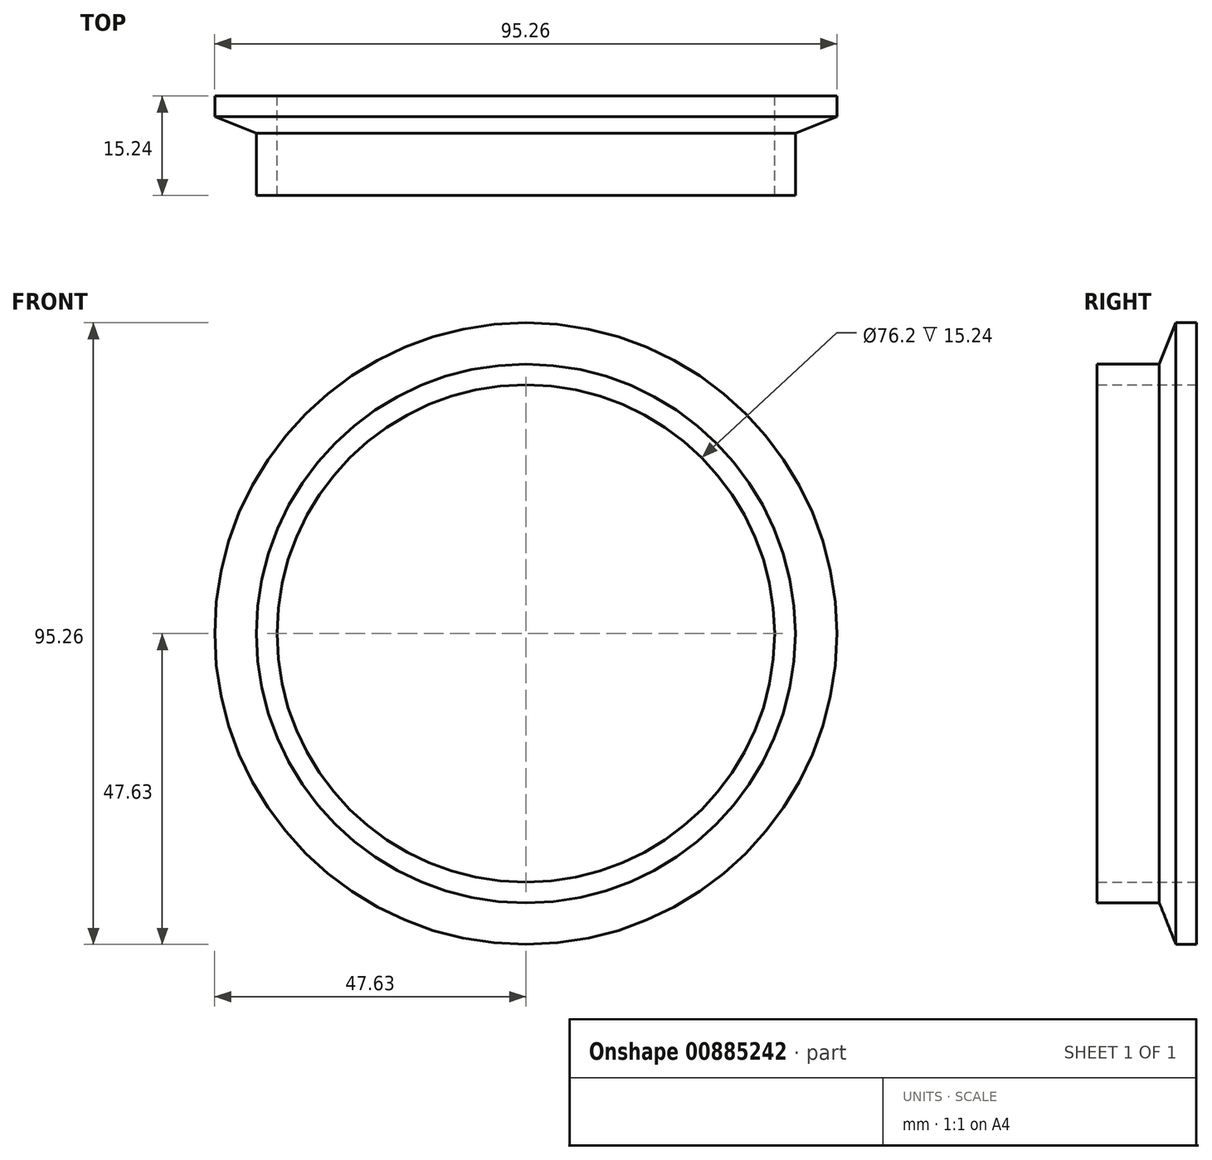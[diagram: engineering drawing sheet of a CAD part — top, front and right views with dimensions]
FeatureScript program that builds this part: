
annotation { "Feature Type Name" : "Feature", "Feature Type Description" : "" }
export const myFeature = defineFeature(function(context is Context, id is Id, definition is map)
    precondition{}
    {
        {
            var Q0;
            Q0=qCreatedBy(makeId("Front.planeOp"),FACE);
            var sketch = newSketch(context, id + "F0", { "sketchPlane" : qUnion([Q0])});
            skCircle(sketch, "E0", {"center": v(0, 0) * mm, "radius": 38.1 * mm});
            skCircle(sketch, "E1", {"center": v(0, 0) * mm, "radius": 47.63 * mm});
            skSolve(sketch);
        }
        {
            var Q0;
            Q0=makeQuery(id+"F0.imprint","IMPRINT",FACE,{"disambiguationData":[TD([[makeQuery(id+"F0.imprint","IMPRINT",EDGE,{"derivedFrom":sQuery(id+"F0.wireOp",EDGE,"E0")}),-1.0]])]});
            extrude(context, id + "F1", {"entities" : qUnion([Q0]), "depth" : 15.24 * mm, "offsetDistance" : 25.4 * mm});
        }
        {
            var Q0;
            Q0=makeQuery(id+"F1.opExtrude","CAP_FACE",FACE,{"disambiguationData":[OSD([sQuery(id+"F0.wireOp",EDGE,"E0"),sQuery(id+"F0.wireOp",EDGE,"E1")])],"isStart":false});
            var sketch = newSketch(context, id + "F2", { "sketchPlane" : qUnion([Q0])});
            skCircle(sketch, "E2", {"center": v(0, 0) * mm, "radius": 41.28 * mm});
            skSolve(sketch);
        }
        {
            var Q0;
            Q0=makeQuery(id+"F2.imprint","IMPRINT",FACE,{"disambiguationData":[TD([[makeQuery(id+"F2.imprint","IMPRINT",EDGE,{"derivedFrom":sQuery(id+"F2.wireOp",EDGE,"E2")}),-1.0]])]});
            extrude(context, id + "F3", {"entities" : qUnion([Q0]), "operationType" : NewBodyOperationType.REMOVE, "oppositeDirection" : true, "depth" : 12.06 * mm, "offsetDistance" : 25.4 * mm});
        }
        {
            var Q0;
            Q0=makeQuery(id+"F3.boolean.opBoolean","COPY",EDGE,{"derivedFrom":makeQuery(id+"F3.opExtrude","CAP_EDGE",EDGE,{"disambiguationData":[OSD([sQuery(id+"F2.wireOp",EDGE,"E2")])],"isStart":false})});
            chamfer(context, id + "F4", {"entities" : qUnion([Q0]), "chamferType" : ChamferType.TWO_OFFSETS, "width1" : 2.54 * mm, "oppositeDirection" : false, "width2" : 6.35 * mm, "tangentPropagation" : true});
        }
    });
